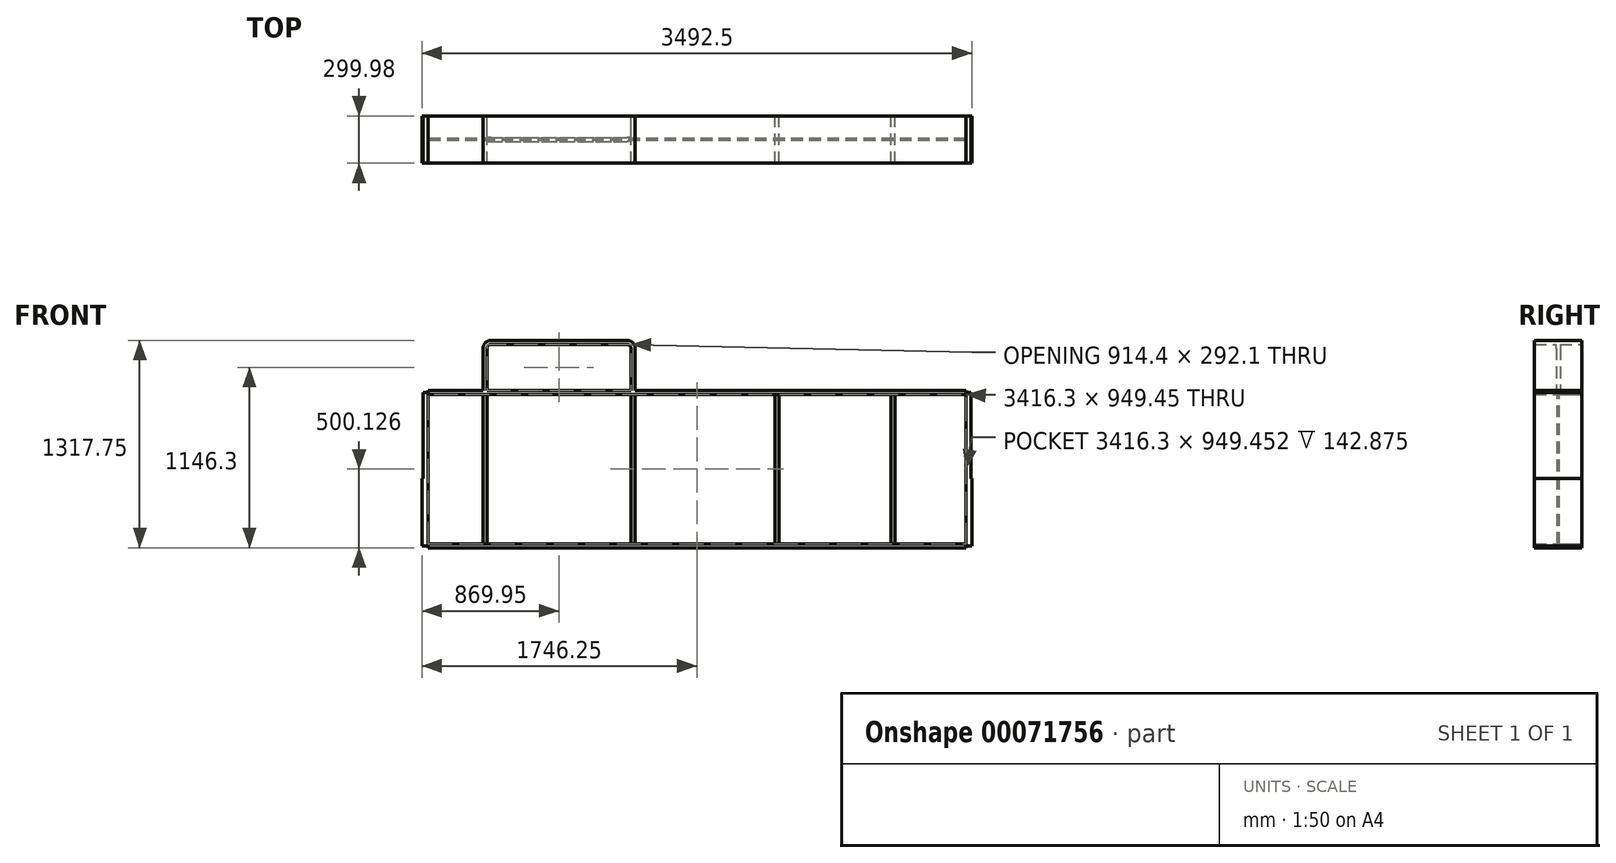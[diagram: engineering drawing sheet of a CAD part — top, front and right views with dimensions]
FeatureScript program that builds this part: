
annotation { "Feature Type Name" : "Feature", "Feature Type Description" : "" }
export const myFeature = defineFeature(function(context is Context, id is Id, definition is map)
    precondition{}
    {
        {
            var Q0;
            Q0=qCreatedBy(makeId("Front.planeOp"),FACE);
            var sketch = newSketch(context, id + "F0", { "sketchPlane" : qUnion([Q0])});
            skLineSegment(sketch, "E0.bottom", {"start": v(-1746.25, 0) * mm, "end": v(1746.25, 0) * mm});
            skLineSegment(sketch, "E0.top", {"start": v(-1746.25, 1000.25) * mm, "end": v(1746.25, 1000.25) * mm});
            skLineSegment(sketch, "E0.left", {"start": v(-1746.25, 0) * mm, "end": v(-1746.25, 1000.25) * mm});
            skLineSegment(sketch, "E0.right", {"start": v(1746.25, 0) * mm, "end": v(1746.25, 1000.25) * mm});
            skSolve(sketch);
        }
        {
            var Q0;
            Q0 = qSketchRegion(id + "F0", true);
            extrude(context, id + "F1", {"entities" : qUnion([Q0]), "endBound" : BoundingType.SYMMETRIC, "depth" : 14.22 * mm});
        }
        {
            var Q0;
            Q0=qCreatedBy(makeId("Front.planeOp"),FACE);
            var sketch = newSketch(context, id + "F2", { "sketchPlane" : qUnion([Q0])});
            skLineSegment(sketch, "E1.bottom", {"start": v(-1708.15, 0) * mm, "end": v(1708.15, 0) * mm});
            skLineSegment(sketch, "E1.top", {"start": v(-1708.15, 25.4) * mm, "end": v(1708.15, 25.4) * mm});
            skLineSegment(sketch, "E1.left", {"start": v(-1708.15, 0) * mm, "end": v(-1708.15, 25.4) * mm});
            skLineSegment(sketch, "E1.right", {"start": v(1708.15, 0) * mm, "end": v(1708.15, 25.4) * mm});
            skLineSegment(sketch, "E2.0", {"start": v(1746.25, 0) * mm, "end": v(1746.25, 1000.25) * mm, "construction": true});
            skLineSegment(sketch, "E3.0", {"start": v(-1746.25, 0) * mm, "end": v(-1746.25, 1000.25) * mm, "construction": true});
            skLineSegment(sketch, "E4", {"start": v(-1746.25, 500.13) * mm, "end": v(1746.25, 500.13) * mm, "construction": true});
            skLineSegment(sketch, "E5.MirrorCS", {"start": v(1708.15, 1000.25) * mm, "end": v(1708.15, 974.85) * mm});
            skLineSegment(sketch, "E6.MirrorCS", {"start": v(-1708.15, 1000.25) * mm, "end": v(-1708.15, 974.85) * mm});
            skLineSegment(sketch, "E7.MirrorCS", {"start": v(-1708.15, 974.85) * mm, "end": v(1708.15, 974.85) * mm});
            skLineSegment(sketch, "E8.MirrorCS", {"start": v(-1708.15, 1000.25) * mm, "end": v(1708.15, 1000.25) * mm});
            skPoint(sketch, "E9.oppositeSnap0", {"position": v(-1708.15, 12.7) * mm});
            skLineSegment(sketch, "E9.bottom", {"start": v(-1708.15, 987.55) * mm, "end": v(-1746.25, 987.55) * mm});
            skLineSegment(sketch, "E9.top", {"start": v(-1708.15, 12.7) * mm, "end": v(-1746.25, 12.7) * mm});
            skLineSegment(sketch, "E9.left", {"start": v(-1708.15, 987.55) * mm, "end": v(-1708.15, 12.7) * mm});
            skLineSegment(sketch, "E9.right", {"start": v(-1746.25, 987.55) * mm, "end": v(-1746.25, 12.7) * mm});
            skLineSegment(sketch, "E10", {"start": v(0, 974.85) * mm, "end": v(0, 25.4) * mm, "construction": true});
            skLineSegment(sketch, "E11.MirrorCS", {"start": v(1708.15, 987.55) * mm, "end": v(1746.25, 987.55) * mm});
            skLineSegment(sketch, "E12.MirrorCS", {"start": v(1708.15, 12.7) * mm, "end": v(1746.25, 12.7) * mm});
            skLineSegment(sketch, "E13.MirrorCS", {"start": v(1746.25, 987.55) * mm, "end": v(1746.25, 12.7) * mm});
            skLineSegment(sketch, "E14.MirrorCS", {"start": v(1708.15, 987.55) * mm, "end": v(1708.15, 12.7) * mm});
            skPoint(sketch, "E15.MirrorP", {"position": v(1708.15, 12.7) * mm});
            skSolve(sketch);
        }
        {
            var Q0;
            Q0 = qSketchRegion(id + "F2", true);
            extrude(context, id + "F3", {"entities" : qUnion([Q0]), "operationType" : NewBodyOperationType.ADD, "endBound" : BoundingType.SYMMETRIC, "depth" : 299.97 * mm});
        }
        {
            var Q0;
            Q0=qCreatedBy(makeId("Front.planeOp"),FACE);
            var sketch = newSketch(context, id + "F4", { "sketchPlane" : qUnion([Q0])});
            skPoint(sketch, "E16.0", {"position": v(-1746.25, 1000.25) * mm});
            skLineSegment(sketch, "E17.bottom", {"start": v(-1746.25, 1000.25) * mm, "end": v(-1739.9, 1000.25) * mm});
            skLineSegment(sketch, "E17.top", {"start": v(-1746.25, 441.45) * mm, "end": v(-1739.9, 441.45) * mm});
            skLineSegment(sketch, "E17.left", {"start": v(-1746.25, 1000.25) * mm, "end": v(-1746.25, 441.45) * mm});
            skLineSegment(sketch, "E17.right", {"start": v(-1739.9, 1000.25) * mm, "end": v(-1739.9, 441.45) * mm});
            skLineSegment(sketch, "E18", {"start": v(0, -58.3) * mm, "end": v(0, 1155.28) * mm, "construction": true});
            skLineSegment(sketch, "E19.MirrorCS", {"start": v(1746.25, 1000.25) * mm, "end": v(1739.9, 1000.25) * mm});
            skLineSegment(sketch, "E20.MirrorCS", {"start": v(1746.25, 441.45) * mm, "end": v(1739.9, 441.45) * mm});
            skPoint(sketch, "E21.MirrorP", {"position": v(1746.25, 1000.25) * mm});
            skLineSegment(sketch, "E22.MirrorCS", {"start": v(1739.9, 1000.25) * mm, "end": v(1739.9, 441.45) * mm});
            skLineSegment(sketch, "E23.MirrorCS", {"start": v(1746.25, 1000.25) * mm, "end": v(1746.25, 441.45) * mm});
            skSolve(sketch);
        }
        {
            var Q0;
            Q0 = qSketchRegion(id + "F4", true);
            extrude(context, id + "F5", {"entities" : qUnion([Q0]), "operationType" : NewBodyOperationType.REMOVE, "endBound" : BoundingType.SYMMETRIC, "oppositeDirection" : true, "depth" : 304.8 * mm});
        }
        {
            var Q0;
            Q0=makeQuery(id+"F3.opExtrude","CAP_FACE",FACE,{"disambiguationData":[OSD([sQuery(id+"F2.wireOp",EDGE,"E1.bottom"),sQuery(id+"F2.wireOp",EDGE,"E1.top"),sQuery(id+"F2.wireOp",EDGE,"E1.left"),sQuery(id+"F2.wireOp",EDGE,"E6.MirrorCS"),sQuery(id+"F2.wireOp",EDGE,"E7.MirrorCS"),sQuery(id+"F2.wireOp",EDGE,"E8.MirrorCS"),sQuery(id+"F2.wireOp",EDGE,"E9.bottom"),sQuery(id+"F2.wireOp",EDGE,"E9.top"),sQuery(id+"F2.wireOp",EDGE,"E9.left"),sQuery(id+"F2.wireOp",EDGE,"E9.right"),sQuery(id+"F2.wireOp",EDGE,"E5.MirrorCS"),sQuery(id+"F2.wireOp",EDGE,"E1.right"),sQuery(id+"F2.wireOp",EDGE,"E11.MirrorCS"),sQuery(id+"F2.wireOp",EDGE,"E12.MirrorCS"),sQuery(id+"F2.wireOp",EDGE,"E13.MirrorCS"),sQuery(id+"F2.wireOp",EDGE,"E14.MirrorCS")])],"isStart":false});
            var sketch = newSketch(context, id + "F6", { "sketchPlane" : qUnion([Q0])});
            skLineSegment(sketch, "E24.bottom", {"start": v(-1708.15, 987.55) * mm, "end": v(-1777.82, 987.55) * mm});
            skLineSegment(sketch, "E24.top", {"start": v(-1708.15, 1019.74) * mm, "end": v(-1777.82, 1019.74) * mm});
            skLineSegment(sketch, "E24.left", {"start": v(-1708.15, 987.55) * mm, "end": v(-1708.15, 1019.74) * mm});
            skLineSegment(sketch, "E24.right", {"start": v(-1777.82, 987.55) * mm, "end": v(-1777.82, 1019.74) * mm});
            skLineSegment(sketch, "E25.bottom", {"start": v(1708.15, 987.55) * mm, "end": v(1769.2, 987.55) * mm});
            skLineSegment(sketch, "E25.top", {"start": v(1708.15, 1033.96) * mm, "end": v(1769.2, 1033.96) * mm});
            skLineSegment(sketch, "E25.left", {"start": v(1708.15, 987.55) * mm, "end": v(1708.15, 1033.96) * mm});
            skLineSegment(sketch, "E25.right", {"start": v(1769.2, 987.55) * mm, "end": v(1769.2, 1033.96) * mm});
            skLineSegment(sketch, "E26.bottom", {"start": v(1708.15, 12.7) * mm, "end": v(1775.25, 12.7) * mm});
            skLineSegment(sketch, "E26.top", {"start": v(1708.15, -29.13) * mm, "end": v(1775.25, -29.13) * mm});
            skLineSegment(sketch, "E26.left", {"start": v(1708.15, 12.7) * mm, "end": v(1708.15, -29.13) * mm});
            skLineSegment(sketch, "E26.right", {"start": v(1775.25, 12.7) * mm, "end": v(1775.25, -29.13) * mm});
            skLineSegment(sketch, "E27.bottom", {"start": v(-1708.15, 12.7) * mm, "end": v(-1780.9, 12.7) * mm});
            skLineSegment(sketch, "E27.top", {"start": v(-1708.15, -36.57) * mm, "end": v(-1780.9, -36.57) * mm});
            skLineSegment(sketch, "E27.left", {"start": v(-1708.15, 12.7) * mm, "end": v(-1708.15, -36.57) * mm});
            skLineSegment(sketch, "E27.right", {"start": v(-1780.9, 12.7) * mm, "end": v(-1780.9, -36.57) * mm});
            skSolve(sketch);
        }
        {
            var Q0;
            Q0 = qSketchRegion(id + "F6", true);
            extrude(context, id + "F7", {"entities" : qUnion([Q0]), "operationType" : NewBodyOperationType.REMOVE, "endBound" : BoundingType.THROUGH_ALL, "oppositeDirection" : true, "depth" : 25.4 * mm});
        }
        {
            var Q0;
            Q0=qCreatedBy(makeId("Front.planeOp"),FACE);
            var sketch = newSketch(context, id + "F8", { "sketchPlane" : qUnion([Q0])});
            skLineSegment(sketch, "E28.0", {"start": v(-876.3, 987.55) * mm, "end": v(-876.3, 441.45) * mm, "construction": true});
            skLineSegment(sketch, "E29.0", {"start": v(876.3, 987.55) * mm, "end": v(876.3, 441.45) * mm, "construction": true});
            skLineSegment(sketch, "E30.0", {"start": v(-1708.15, 25.4) * mm, "end": v(1708.15, 25.4) * mm});
            skLineSegment(sketch, "E31.0", {"start": v(-1333.5, 1317.75) * mm, "end": v(-1333.5, 25.4) * mm});
            skLineSegment(sketch, "E32.0", {"start": v(-1358.9, 1266.95) * mm, "end": v(-1358.9, 25.4) * mm});
            skLineSegment(sketch, "E33.0", {"start": v(-1308.1, 1317.75) * mm, "end": v(-444.5, 1317.75) * mm});
            skLineSegment(sketch, "E34.0", {"start": v(-1308.1, 1292.35) * mm, "end": v(-444.5, 1292.35) * mm});
            skLineSegment(sketch, "E34.1", {"start": v(-1333.5, 1266.95) * mm, "end": v(-1333.5, 25.4) * mm});
            skLineSegment(sketch, "E35.MirrorCS", {"start": v(-419.1, 1266.95) * mm, "end": v(-419.1, 25.4) * mm});
            skLineSegment(sketch, "E36.MirrorCS", {"start": v(-393.7, 1266.95) * mm, "end": v(-393.7, 25.4) * mm});
            skLineSegment(sketch, "E37.MirrorCS", {"start": v(-419.1, 1292.35) * mm, "end": v(-419.1, 25.4) * mm});
            skPoint(sketch, "E38.visualSharp", {"position": v(-1333.5, 1292.35) * mm});
            skArc(sketch, "E38.filletArc", {"start": v(-1308.1, 1292.35) * mm, "mid": v(-1326.06, 1284.91) * mm, "end": v(-1333.5, 1266.95) * mm});
            skPoint(sketch, "E39.newPointB", {"position": v(-419.1, 1317.75) * mm});
            skArc(sketch, "E39.filletArc", {"start": v(-419.1, 1266.95) * mm, "mid": v(-426.54, 1284.91) * mm, "end": v(-444.5, 1292.35) * mm});
            skPoint(sketch, "E40.visualSharp", {"position": v(-1358.9, 1317.75) * mm});
            skArc(sketch, "E40.filletArc", {"start": v(-1308.1, 1317.75) * mm, "mid": v(-1344.02, 1302.87) * mm, "end": v(-1358.9, 1266.95) * mm});
            skPoint(sketch, "E41.visualSharp", {"position": v(-393.7, 1317.75) * mm});
            skArc(sketch, "E41.filletArc", {"start": v(-393.7, 1266.95) * mm, "mid": v(-408.58, 1302.87) * mm, "end": v(-444.5, 1317.75) * mm});
            skLineSegment(sketch, "E42", {"start": v(0, 1077.49) * mm, "end": v(0, -160.54) * mm, "construction": true});
            skLineSegment(sketch, "E43.0", {"start": v(-1708.15, 974.85) * mm, "end": v(1708.15, 974.85) * mm});
            skLineSegment(sketch, "E44.0.1", {"start": v(1708.15, 25.4) * mm, "end": v(1708.15, 974.85) * mm});
            skLineSegment(sketch, "E44.0.2", {"start": v(1708.15, 974.85) * mm, "end": v(-1708.15, 974.85) * mm});
            skLineSegment(sketch, "E44.0.3", {"start": v(-1708.15, 974.85) * mm, "end": v(-1708.15, 25.4) * mm});
            skLineSegment(sketch, "E45.0", {"start": v(520.7, 974.85) * mm, "end": v(520.7, 25.4) * mm});
            skLineSegment(sketch, "E46.0", {"start": v(495.3, 974.85) * mm, "end": v(495.3, 25.4) * mm});
            skLineSegment(sketch, "E47.MirrorCS", {"start": v(1231.9, 974.85) * mm, "end": v(1231.9, 25.4) * mm});
            skLineSegment(sketch, "E48.MirrorCS", {"start": v(1257.3, 974.85) * mm, "end": v(1257.3, 25.4) * mm});
            skSolve(sketch);
        }
        {
            var Q0;
            Q0=makeQuery(id+"F8.imprint","IMPRINT",FACE,{"disambiguationData":[TD([[makeQuery(id+"F8.imprint","IMPRINT",EDGE,{"derivedFrom":sQuery(id+"F8.wireOp",EDGE,"E34.0")}),-1.0]])]});
            extrude(context, id + "F9", {"entities" : qUnion([Q0]), "operationType" : NewBodyOperationType.ADD, "endBound" : BoundingType.SYMMETRIC, "depth" : 25.4 * mm});
        }
        {
            var Q0;
            {var subQ0=sQuery(id+"F8.wireOp",EDGE,"E40.filletArc");var subQ1=sQuery(id+"F8.wireOp",EDGE,"E32.0");var subQ2=makeQuery(id+"F8.imprint","INTERSECT",VERTEX,{"derivedFrom":[subQ1,subQ0]});Q0=makeQuery(id+"F8.imprint","IMPRINT",FACE,{"disambiguationData":[TD([[makeQuery(id+"F8.imprint","IMPRINT",EDGE,{"disambiguationData":[TD([[subQ2,-1.0]])],"derivedFrom":subQ1}),1.0]])]});}
            var Q1;
            {var subQ7=sQuery(id+"F8.wireOp",EDGE,"E33.0");Q1=makeQuery(id+"F8.imprint","IMPRINT",FACE,{"disambiguationData":[TD([[makeQuery(id+"F8.imprint","IMPRINT",EDGE,{"derivedFrom":subQ7}),-1.0]])]});}
            extrude(context, id + "F10", {"entities" : qUnion([Q0, Q1]), "operationType" : NewBodyOperationType.ADD, "endBound" : BoundingType.SYMMETRIC, "depth" : 299.97 * mm});
        }
        {
            var Q0;
            {var subQ0=sQuery(id+"F8.wireOp",EDGE,"E30.0");var subQ1=sQuery(id+"F8.wireOp",EDGE,"E32.0");var subQ2=makeQuery(id+"F8.imprint","INTERSECT",VERTEX,{"derivedFrom":[subQ1,subQ0]});Q0=makeQuery(id+"F8.imprint","IMPRINT",FACE,{"disambiguationData":[TD([[makeQuery(id+"F8.imprint","IMPRINT",EDGE,{"disambiguationData":[TD([[subQ2,1.0]])],"derivedFrom":subQ1}),1.0]])]});}
            var Q1;
            {var subQ0=sQuery(id+"F8.wireOp",EDGE,"E30.0");var subQ1=sQuery(id+"F8.wireOp",EDGE,"E36.MirrorCS");var subQ2=makeQuery(id+"F8.imprint","INTERSECT",VERTEX,{"derivedFrom":[subQ1,subQ0]});Q1=makeQuery(id+"F8.imprint","IMPRINT",FACE,{"disambiguationData":[TD([[makeQuery(id+"F8.imprint","IMPRINT",EDGE,{"disambiguationData":[TD([[subQ2,1.0]])],"derivedFrom":subQ1}),-1.0]])]});}
            var Q2;
            {var subQ0=sQuery(id+"F8.wireOp",EDGE,"E45.0");Q2=makeQuery(id+"F8.imprint","IMPRINT",FACE,{"disambiguationData":[TD([[makeQuery(id+"F8.imprint","IMPRINT",EDGE,{"derivedFrom":subQ0}),-1.0]])]});}
            var Q3;
            {var subQ0=sQuery(id+"F8.wireOp",EDGE,"E47.MirrorCS");Q3=makeQuery(id+"F8.imprint","IMPRINT",FACE,{"disambiguationData":[TD([[makeQuery(id+"F8.imprint","IMPRINT",EDGE,{"derivedFrom":subQ0}),1.0]])]});}
            extrude(context, id + "F11", {"entities" : qUnion([Q0, Q1, Q2, Q3]), "endBound" : BoundingType.SYMMETRIC, "depth" : 299.97 * mm});
        }
    });
